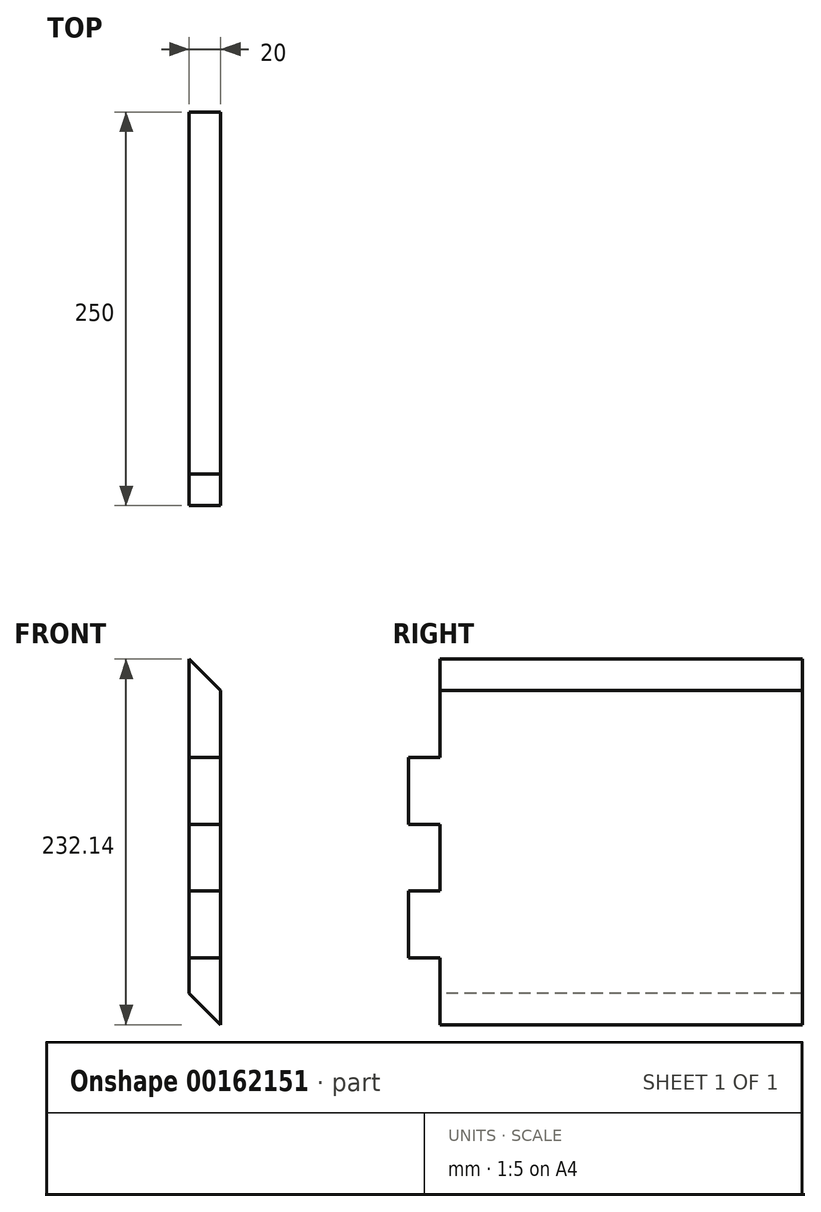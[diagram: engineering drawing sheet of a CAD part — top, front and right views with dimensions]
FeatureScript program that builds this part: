
annotation { "Feature Type Name" : "Feature", "Feature Type Description" : "" }
export const myFeature = defineFeature(function(context is Context, id is Id, definition is map)
    precondition{}
    {
        {
            assignVariable(context, id + "F0", {"name" : "L", "anyValue" : 250 * mm});
        }
        {
            assignVariable(context, id + "F1", {"name" : "t", "anyValue" : 20 * mm});
        }
        {
            var Q0;
            Q0=qCreatedBy(makeId("Right.planeOp"),FACE);
            var sketch = newSketch(context, id + "F2", { "sketchPlane" : qUnion([Q0])});
            skLineSegment(sketch, "E0.bottom", {"start": v(125, 116.07) * mm, "end": v(-125, 116.07) * mm});
            skLineSegment(sketch, "E0.top", {"start": v(125, -116.07) * mm, "end": v(-125, -116.07) * mm});
            skLineSegment(sketch, "E0.left", {"start": v(125, 116.07) * mm, "end": v(125, -116.07) * mm});
            skLineSegment(sketch, "E0.right", {"start": v(-125, 116.07) * mm, "end": v(-125, -116.07) * mm});
            skPoint(sketch, "E0.middle", {"position": v(0, 0) * mm});
            skSolve(sketch);
        }
        {
            var Q0;
            Q0=qSketchRegion(id+"F2",true);
            extrude(context, id + "F3", {"entities" : qUnion([Q0]), "endBound" : BoundingType.SYMMETRIC, "depth" : getVariable(context, 't')});
        }
        {
            var Q0;
            Q0=qCreatedBy(makeId("Front.planeOp"),FACE);
            var sketch = newSketch(context, id + "F4", { "sketchPlane" : qUnion([Q0])});
            skLineSegment(sketch, "E1", {"start": v(-10, 116.07) * mm, "end": v(10, 116.07) * mm});
            skLineSegment(sketch, "E2", {"start": v(10, 116.07) * mm, "end": v(10, 96.07) * mm});
            skLineSegment(sketch, "E3", {"start": v(10, 96.07) * mm, "end": v(-10, 116.07) * mm});
            skLineSegment(sketch, "E4", {"start": v(10, -116.07) * mm, "end": v(-10, -96.07) * mm});
            skLineSegment(sketch, "E5", {"start": v(-10, -96.07) * mm, "end": v(-10, -116.07) * mm});
            skLineSegment(sketch, "E6", {"start": v(-10, -116.07) * mm, "end": v(10, -116.07) * mm});
            skSolve(sketch);
        }
        {
            var Q0;
            Q0 = qSketchRegion(id + "F4", true);
            extrude(context, id + "F5", {"entities" : qUnion([Q0]), "operationType" : NewBodyOperationType.REMOVE, "endBound" : BoundingType.SYMMETRIC, "oppositeDirection" : true, "depth" : getVariable(context, 'L')});
        }
        {
            var Q0;
            Q0=makeQuery(id+"F3.opExtrude","SWEPT_FACE",FACE,{"disambiguationData":[OSD([sQuery(id+"F2.wireOp",EDGE,"E0.right")])]});
            var sketch = newSketch(context, id + "F6", { "sketchPlane" : qUnion([Q0])});
            skLineSegment(sketch, "E7.bottom", {"start": v(10, 96.07) * mm, "end": v(-10, 96.07) * mm, "construction": true});
            skLineSegment(sketch, "E7.top", {"start": v(10, 53.64) * mm, "end": v(-10, 53.64) * mm});
            skLineSegment(sketch, "E7.left", {"start": v(10, 96.07) * mm, "end": v(10, 53.64) * mm});
            skLineSegment(sketch, "E7.right", {"start": v(-10, 96.07) * mm, "end": v(-10, 53.64) * mm});
            skLineSegment(sketch, "E8.bottom", {"start": v(10, 11.21) * mm, "end": v(-10, 11.21) * mm});
            skLineSegment(sketch, "E8.left", {"start": v(10, 11.21) * mm, "end": v(10, -31.21) * mm});
            skLineSegment(sketch, "E8.right", {"start": v(-10, 11.21) * mm, "end": v(-10, -31.21) * mm});
            skLineSegment(sketch, "E9.bottom", {"start": v(-10, -73.64) * mm, "end": v(10, -73.64) * mm});
            skLineSegment(sketch, "E9.top", {"start": v(-10, -116.07) * mm, "end": v(10, -116.07) * mm});
            skLineSegment(sketch, "E9.left", {"start": v(-10, -73.64) * mm, "end": v(-10, -116.07) * mm});
            skLineSegment(sketch, "E9.right", {"start": v(10, -73.64) * mm, "end": v(10, -116.07) * mm});
            skLineSegment(sketch, "E10", {"start": v(10, 53.64) * mm, "end": v(10, 11.21) * mm, "construction": true});
            skLineSegment(sketch, "E11", {"start": v(10, -31.21) * mm, "end": v(10, -73.64) * mm, "construction": true});
            skLineSegment(sketch, "E12", {"start": v(-10, -31.21) * mm, "end": v(10, -31.21) * mm});
            skLineSegment(sketch, "E13", {"start": v(-10, 96.07) * mm, "end": v(-10, 116.07) * mm});
            skLineSegment(sketch, "E14", {"start": v(-10, 116.07) * mm, "end": v(10, 96.07) * mm});
            skSolve(sketch);
        }
        {
            var Q0;
            Q0 = qSketchRegion(id + "F6", true);
            extrude(context, id + "F7", {"entities" : qUnion([Q0]), "operationType" : NewBodyOperationType.REMOVE, "oppositeDirection" : true, "depth" : getVariable(context, 't')});
        }
    });
